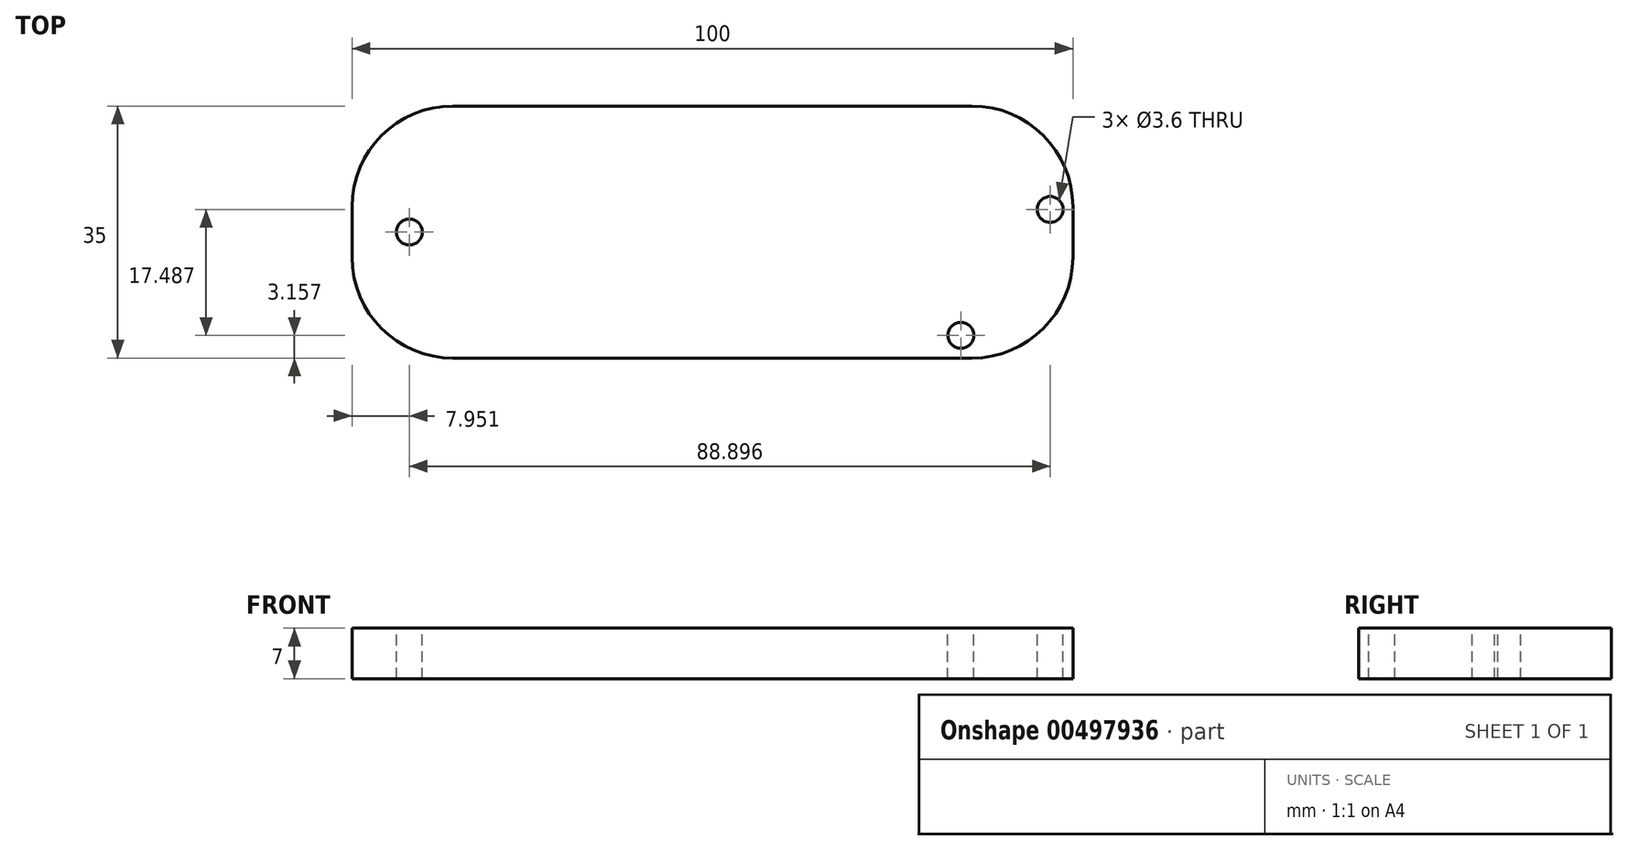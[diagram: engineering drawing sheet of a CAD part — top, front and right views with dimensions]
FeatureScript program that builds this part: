
annotation { "Feature Type Name" : "Feature", "Feature Type Description" : "" }
export const myFeature = defineFeature(function(context is Context, id is Id, definition is map)
    precondition{}
    {
        {
            var Q0;
            Q0=qCreatedBy(makeId("Top.planeOp"),FACE);
            var sketch = newSketch(context, id + "F0", { "sketchPlane" : qUnion([Q0])});
            skLineSegment(sketch, "E0.bottom", {"start": v(36, 17.5) * mm, "end": v(-36, 17.5) * mm});
            skLineSegment(sketch, "E0.top", {"start": v(36, -17.5) * mm, "end": v(-36, -17.5) * mm});
            skLineSegment(sketch, "E0.left", {"start": v(50, 3.5) * mm, "end": v(50, -3.5) * mm});
            skLineSegment(sketch, "E0.right", {"start": v(-50, 3.5) * mm, "end": v(-50, -3.5) * mm});
            skPoint(sketch, "E0.middle", {"position": v(0, 0) * mm});
            skPoint(sketch, "E1.visualSharp", {"position": v(-50, 17.5) * mm});
            skArc(sketch, "E1.filletArc", {"start": v(-36, 17.5) * mm, "mid": v(-45.9, 13.4) * mm, "end": v(-50, 3.5) * mm});
            skPoint(sketch, "E2.visualSharp", {"position": v(-50, -17.5) * mm});
            skArc(sketch, "E2.filletArc", {"start": v(-50, -3.5) * mm, "mid": v(-45.9, -13.4) * mm, "end": v(-36, -17.5) * mm});
            skPoint(sketch, "E3.visualSharp", {"position": v(50, 17.5) * mm});
            skArc(sketch, "E3.filletArc", {"start": v(50, 3.5) * mm, "mid": v(45.9, 13.4) * mm, "end": v(36, 17.5) * mm});
            skPoint(sketch, "E4.visualSharp", {"position": v(50, -17.5) * mm});
            skArc(sketch, "E4.filletArc", {"start": v(36, -17.5) * mm, "mid": v(45.9, -13.4) * mm, "end": v(50, -3.5) * mm});
            skSolve(sketch);
        }
        {
            var Q0;
            Q0 = qSketchRegion(id + "F0", true);
            extrude(context, id + "F1", {"entities" : qUnion([Q0]), "endBound" : BoundingType.SYMMETRIC, "depth" : 7 * mm});
        }
        {
            var Q0;
            Q0=makeQuery(id+"F1.opExtrude","CAP_FACE",FACE,{"disambiguationData":[OSD([sQuery(id+"F0.wireOp",EDGE,"E0.bottom"),sQuery(id+"F0.wireOp",EDGE,"E0.top"),sQuery(id+"F0.wireOp",EDGE,"E0.left"),sQuery(id+"F0.wireOp",EDGE,"E0.right")])],"isStart":false});
            var sketch = newSketch(context, id + "F2", { "sketchPlane" : qUnion([Q0])});
            skCircle(sketch, "E5", {"center": v(-42.05, 0) * mm, "radius": 1.8 * mm});
            skPoint(sketch, "E5.centerSnap0", {"position": v(-50, 0) * mm});
            skSolve(sketch);
        }
        {
            var Q0;
            Q0 = qSketchRegion(id + "F2", true);
            extrude(context, id + "F3", {"entities" : qUnion([Q0]), "operationType" : NewBodyOperationType.REMOVE, "oppositeDirection" : true, "depth" : 11 * mm});
        }
        {
            var Q0;
            Q0=makeQuery(id+"F1.opExtrude","CAP_FACE",FACE,{"disambiguationData":[OSD([sQuery(id+"F0.wireOp",EDGE,"E0.bottom"),sQuery(id+"F0.wireOp",EDGE,"E0.top"),sQuery(id+"F0.wireOp",EDGE,"E0.left"),sQuery(id+"F0.wireOp",EDGE,"E0.right"),sQuery(id+"F0.wireOp",EDGE,"E1.filletArc"),sQuery(id+"F0.wireOp",EDGE,"E2.filletArc"),sQuery(id+"F0.wireOp",EDGE,"E3.filletArc"),sQuery(id+"F0.wireOp",EDGE,"E4.filletArc")])],"isStart":false});
            var sketch = newSketch(context, id + "F4", { "sketchPlane" : qUnion([Q0])});
            skPoint(sketch, "E6.centerSnap0", {"position": v(45.9, -13.4) * mm});
            skCircle(sketch, "E7", {"center": v(46.85, 3.14) * mm, "radius": 1.8 * mm});
            skPoint(sketch, "E7.centerSnap0", {"position": v(45.9, 13.4) * mm});
            skCircle(sketch, "E8", {"center": v(34.45, -14.34) * mm, "radius": 1.8 * mm});
            skSolve(sketch);
        }
        {
            var Q0;
            Q0 = qSketchRegion(id + "F4", true);
            extrude(context, id + "F5", {"entities" : qUnion([Q0]), "operationType" : NewBodyOperationType.REMOVE, "oppositeDirection" : true, "depth" : 7 * mm});
        }
    });
